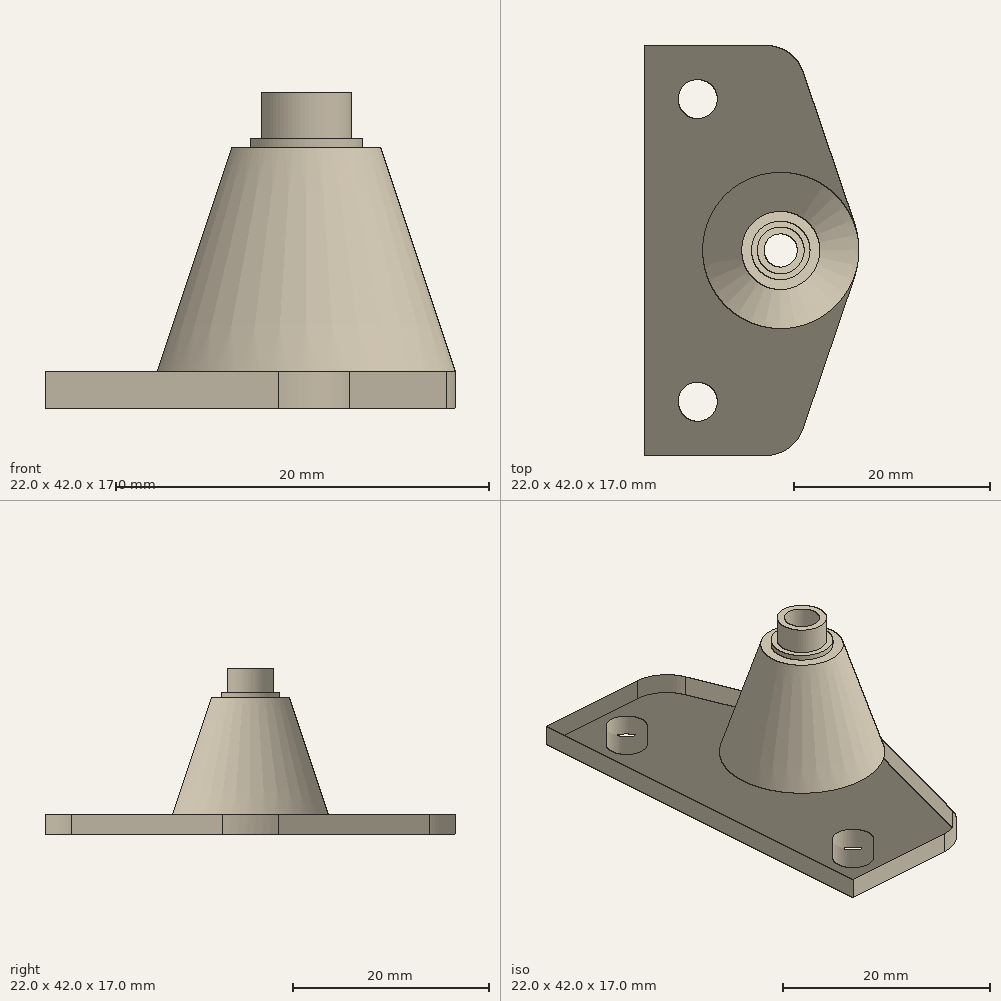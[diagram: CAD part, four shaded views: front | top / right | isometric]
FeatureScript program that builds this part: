
annotation { "Feature Type Name" : "Feature", "Feature Type Description" : "" }
export const myFeature = defineFeature(function(context is Context, id is Id, definition is map)
    precondition{}
    {
        {
            var Q0;
            Q0=makeQuery(id+"FVIbtQBJsF2XmXW.importOp","IMPORT",FACE,{"importTag":0.0});
            cPoint(context, id + "F0", {"pointType" : PointType.MESH_POINT, "mesh" : qUnion([Q0]), "x" : -7.44 * mm, "y" : -16 * mm, "z" : -8.5 * mm});
        }
        {
            var Q0;
            Q0=makeQuery(id+"FVIbtQBJsF2XmXW.importOp","IMPORT",FACE,{"importTag":0.0});
            cPoint(context, id + "F1", {"pointType" : PointType.MESH_POINT, "mesh" : qUnion([Q0]), "x" : 1.35 * mm, "y" : -0.42 * mm, "z" : -8.5 * mm});
        }
        {
            var Q0;
            Q0=makeQuery(id+"FVIbtQBJsF2XmXW.importOp","IMPORT",FACE,{"importTag":0.0});
            cPoint(context, id + "F2", {"pointType" : PointType.MESH_POINT, "mesh" : qUnion([Q0]), "x" : -7.44 * mm, "y" : 15 * mm, "z" : -8.5 * mm});
        }
        {
            var Q0;
            Q0 = qCreatedBy(id + "F0" ,VERTEX);
            var Q1;
            Q1 = qCreatedBy(id + "F1" ,VERTEX);
            var Q2;
            Q2 = qCreatedBy(id + "F2" ,VERTEX);
            cPlane(context, id + "F3", {"entities" : qUnion([Q0, Q1, Q2]), "cplaneType" : CPlaneType.THREE_POINT, "offset" : 25 * mm, "width" : 150 * mm, "height" : 150 * mm});
        }
        {
            var Q0;
            Q0=qCreatedBy(id+"F3.planeOp",FACE);
            var sketch = newSketch(context, id + "F4", { "sketchPlane" : qUnion([Q0])});
            skLineSegment(sketch, "E0", {"start": v(-11.02, 21) * mm, "end": v(-11.02, 0) * mm});
            skLineSegment(sketch, "E1", {"start": v(-11.02, 21) * mm, "end": v(1.48, 21) * mm});
            skLineSegment(sketch, "E2", {"start": v(5.27, 18.29) * mm, "end": v(10.5, 2.9) * mm});
            skArc(sketch, "E3", {"start": v(5.27, 18.29) * mm, "mid": v(3.8, 20.25) * mm, "end": v(1.48, 21) * mm});
            skArc(sketch, "E4", {"start": v(10.98, 0) * mm, "mid": v(10.86, 1.47) * mm, "end": v(10.5, 2.9) * mm});
            skArc(sketch, "E5.MirrorCS", {"start": v(10.98, 0) * mm, "mid": v(10.86, -1.47) * mm, "end": v(10.5, -2.9) * mm});
            skLineSegment(sketch, "E6.MirrorCS", {"start": v(-11.02, -21) * mm, "end": v(-11.02, 0) * mm});
            skLineSegment(sketch, "E7.MirrorCS", {"start": v(5.27, -18.29) * mm, "end": v(10.5, -2.9) * mm});
            skArc(sketch, "E8.MirrorCS", {"start": v(5.27, -18.29) * mm, "mid": v(3.8, -20.25) * mm, "end": v(1.48, -21) * mm});
            skLineSegment(sketch, "E9.MirrorCS", {"start": v(-11.02, -21) * mm, "end": v(1.48, -21) * mm});
            skCircle(sketch, "E10", {"center": v(-5.52, 15.5) * mm, "radius": 2 * mm});
            skPoint(sketch, "E10.first.point", {"position": v(-3.54, 15.22) * mm});
            skPoint(sketch, "E10.second.point", {"position": v(-5.9, 13.53) * mm});
            skPoint(sketch, "E10.third.point", {"position": v(-6.97, 16.88) * mm});
            skCircle(sketch, "E11", {"center": v(-5.52, -15.5) * mm, "radius": 2 * mm});
            skCircle(sketch, "E12", {"center": v(2.98, 0) * mm, "radius": 1.7 * mm});
            skPoint(sketch, "E12.first.point", {"position": v(4.36, 1) * mm});
            skPoint(sketch, "E12.second.point", {"position": v(2.9, -1.7) * mm});
            skPoint(sketch, "E12.third.point", {"position": v(1.48, 0.8) * mm});
            skSolve(sketch);
        }
        {
            var Q0;
            Q0 = qSketchRegion(id + "F4", true);
            extrude(context, id + "F5", {"entities" : qUnion([Q0]), "oppositeDirection" : true, "depth" : 2 * mm, "offsetDistance" : 25 * mm});
        }
        {
            var Q0;
            Q0=makeQuery(id+"F5.opExtrude","CAP_FACE",FACE,{"disambiguationData":[OSD([sQuery(id+"F4.wireOp",EDGE,"E0"),sQuery(id+"F4.wireOp",EDGE,"E1"),sQuery(id+"F4.wireOp",EDGE,"E2"),sQuery(id+"F4.wireOp",EDGE,"E3"),sQuery(id+"F4.wireOp",EDGE,"E4"),sQuery(id+"F4.wireOp",EDGE,"E5.MirrorCS"),sQuery(id+"F4.wireOp",EDGE,"E6.MirrorCS"),sQuery(id+"F4.wireOp",EDGE,"E7.MirrorCS"),sQuery(id+"F4.wireOp",EDGE,"E8.MirrorCS"),sQuery(id+"F4.wireOp",EDGE,"E9.MirrorCS"),sQuery(id+"F4.wireOp",EDGE,"E10"),sQuery(id+"F4.wireOp",EDGE,"E11"),sQuery(id+"F4.wireOp",EDGE,"E12")])],"isStart":false});
            var sketch = newSketch(context, id + "F6", { "sketchPlane" : qUnion([Q0])});
            skCircle(sketch, "E13", {"center": v(2.98, 0) * mm, "radius": 8 * mm});
            skSolve(sketch);
        }
        {
            var Q0;
            Q0=makeQuery(id+"FVIbtQBJsF2XmXW.importOp","IMPORT",FACE,{"importTag":0.0});
            cPoint(context, id + "F7", {"pointType" : PointType.MESH_POINT, "mesh" : qUnion([Q0]), "x" : 1.07 * mm, "y" : 3.5 * mm, "z" : 5.5 * mm});
        }
        {
            var Q0;
            Q0=makeQuery(id+"FVIbtQBJsF2XmXW.importOp","IMPORT",FACE,{"importTag":0.0});
            cPoint(context, id + "F8", {"pointType" : PointType.MESH_POINT, "mesh" : qUnion([Q0]), "x" : 1.53 * mm, "y" : -3.72 * mm, "z" : 5.5 * mm});
        }
        {
            var Q0;
            Q0=makeQuery(id+"FVIbtQBJsF2XmXW.importOp","IMPORT",FACE,{"importTag":0.0});
            cPoint(context, id + "F9", {"pointType" : PointType.MESH_POINT, "mesh" : qUnion([Q0]), "x" : 5.14 * mm, "y" : -3.38 * mm, "z" : 5.5 * mm});
        }
        {
            var Q0;
            Q0 = qCreatedBy(id + "F7" ,VERTEX);
            var Q1;
            Q1 = qCreatedBy(id + "F8" ,VERTEX);
            var Q2;
            Q2 = qCreatedBy(id + "F9" ,VERTEX);
            cPlane(context, id + "F10", {"entities" : qUnion([Q0, Q1, Q2]), "cplaneType" : CPlaneType.THREE_POINT, "offset" : 25 * mm, "width" : 150 * mm, "height" : 150 * mm});
        }
        {
            var Q0;
            Q0=qCreatedBy(id+"F10.planeOp",FACE);
            var sketch = newSketch(context, id + "F11", { "sketchPlane" : qUnion([Q0])});
            skCircle(sketch, "E14", {"center": v(2.98, 0) * mm, "radius": 4 * mm});
            skSolve(sketch);
        }
        {
            var Q1;
            Q1 = qSketchRegion(id + "F6", true);
            var Q2;
            Q2 = qSketchRegion(id + "F11", true);
            loft(context, id + "F12", {"operationType" : NewBodyOperationType.ADD, "sheetProfilesArray" : [{ "sheetProfileEntities" : qUnion([Q1]) }, { "sheetProfileEntities" : qUnion([Q2]) }]});
        }
        {
            var Q0;
            Q0=makeQuery(id+"F12.opLoft","CAP_FACE",FACE,{"disambiguationData":[OSD([makeQuery(id+"F11.imprint","IMPRINT",FACE,{"disambiguationData":[TD([[makeQuery(id+"F11.imprint","IMPRINT",EDGE,{"derivedFrom":sQuery(id+"F11.wireOp",EDGE,"E14")}),1.0]])]})])],"isStart":true});
            var sketch = newSketch(context, id + "F13", { "sketchPlane" : qUnion([Q0])});
            skCircle(sketch, "E15", {"center": v(2.98, 0) * mm, "radius": 3 * mm});
            skSolve(sketch);
        }
        {
            var Q0;
            Q0 = qSketchRegion(id + "F13", true);
            extrude(context, id + "F14", {"entities" : qUnion([Q0]), "operationType" : NewBodyOperationType.ADD, "depth" : 0.5 * mm, "offsetDistance" : 25 * mm});
        }
        {
            var Q0;
            Q0=makeQuery(id+"F14.opExtrude","CAP_FACE",FACE,{"disambiguationData":[OSD([sQuery(id+"F13.wireOp",EDGE,"E15")])],"isStart":false});
            var sketch = newSketch(context, id + "F15", { "sketchPlane" : qUnion([Q0])});
            skCircle(sketch, "E16", {"center": v(2.98, 0) * mm, "radius": 2.4 * mm});
            skSolve(sketch);
        }
        {
            var Q0;
            Q0 = qSketchRegion(id + "F15", true);
            extrude(context, id + "F16", {"entities" : qUnion([Q0]), "operationType" : NewBodyOperationType.ADD, "depth" : 2.5 * mm, "offsetDistance" : 25 * mm});
        }
        {
            var Q0;
            Q0=makeQuery(id+"F12.opLoft","CAP_FACE",FACE,{"disambiguationData":[OSD([makeQuery(id+"F6.imprint","IMPRINT",FACE,{"disambiguationData":[TD([[makeQuery(id+"F6.imprint","IMPRINT",EDGE,{"derivedFrom":sQuery(id+"F6.wireOp",EDGE,"E13")}),1.0]])]})])],"isStart":true});
            extrude(context, id + "F17", {"entities" : qUnion([Q0]), "operationType" : NewBodyOperationType.REMOVE, "endBound" : BoundingType.THROUGH_ALL, "oppositeDirection" : true, "depth" : 25 * mm, "offsetDistance" : 25 * mm});
        }
    });
